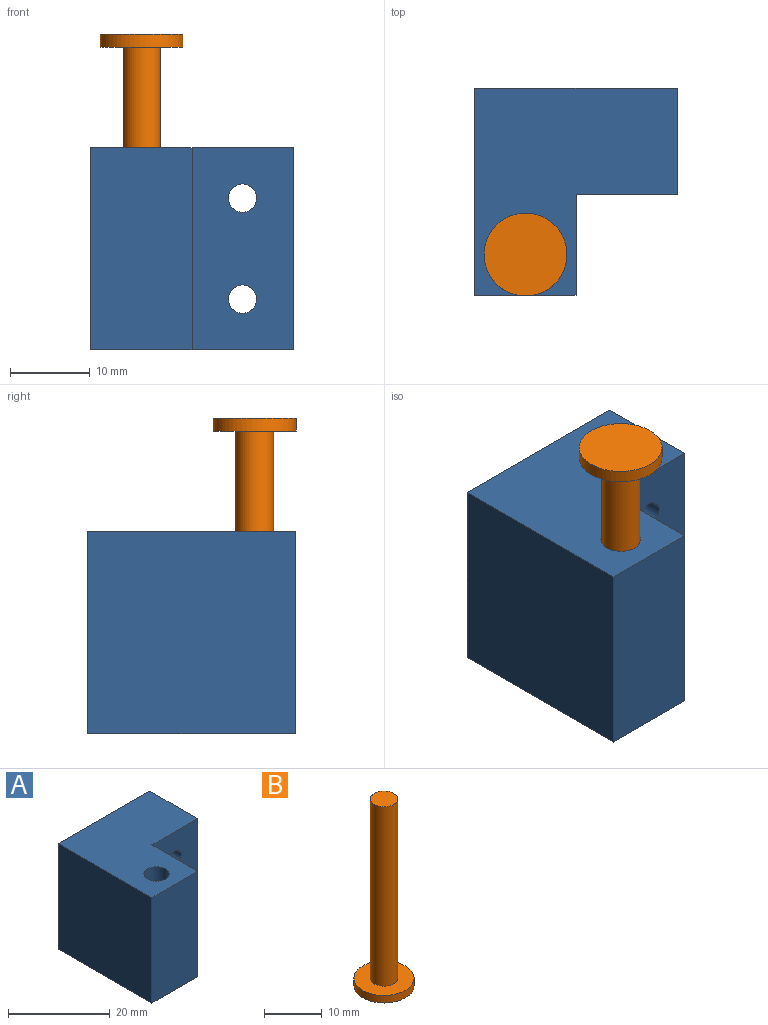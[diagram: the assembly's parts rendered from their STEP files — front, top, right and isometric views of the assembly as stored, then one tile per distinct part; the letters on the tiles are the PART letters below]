
ASSEMBLY  parts=2 mates=1
PART A: 11 faces, bbox 25.4x26x25.4 mm
  f0: plane 26.04x25.4mm, normal (-1,0,0), area 661.3mm2, adj f1,f3,f4,f8
  f1: plane 26.04x25.4mm, normal (0,0,-1), area 480.7mm2, adj f0,f2,f4,f5,f6,f7,f8
  f2: plane 25.4x12.7mm, normal (1,0,0), area 322.6mm2, adj f1,f3,f4,f6
  f3: plane 26.04x25.4mm, normal (0,0,1), area 480.7mm2, adj f0,f2,f4,f5,f6,f7,f8
  f4: plane 25.4x12.7mm, normal (0,-1,0), area 322.6mm2, adj f0,f1,f2,f3
  f5: cylinder r=2.48mm len=25.4mm, axis (0,0,1), area 395.2mm2, adj f1,f3
  f6: plane 25.4x12.7mm, normal (0,-1,0), area 302.7mm2, adj f1,f2,f3,f7,f9,f10
  f7: plane 25.4x13.34mm, normal (1,0,0), area 338.7mm2, adj f1,f3,f6,f8
  f8: plane 25.4x25.4mm, normal (0,1,0), area 625.3mm2, adj f0,f1,f3,f7,f9,f10
  f9: cylinder r=1.78mm len=13.34mm, axis (0,-1,0), area 149mm2, adj f6,f8
  f10: cylinder r=1.78mm len=13.34mm, axis (0,-1,0), area 149mm2, adj f6,f8
PART B: 5 faces, bbox 10.4x10.4x39.6 mm
  f0: plane 10.41x10.41mm, normal (0,0,-1), area 85.2mm2, adj f1
  f1: cylinder r=5.21mm len=10.41mm, axis (0,0,1), area 51.9mm2, adj f0,f2
  f2: plane 10.41x10.41mm, normal (0,0,1), area 67.4mm2, adj f1,f3
  f3: cylinder r=2.38mm len=38.04mm, axis (0,0,1), area 569.1mm2, adj f2,f4
  f4: plane 4.76x4.76mm, normal (0,0,1), area 17.8mm2, adj f3
PLACE A t=(-51.78,3.36,51.22)mm
PLACE B rot(axis=(1,0,0),180deg) t=(-45.43,-4.26,90.84)mm
MATE slider B.f1 <-> A.f5  axis (0,0,-1) through (-45.43,-4.26,51.22)mm
